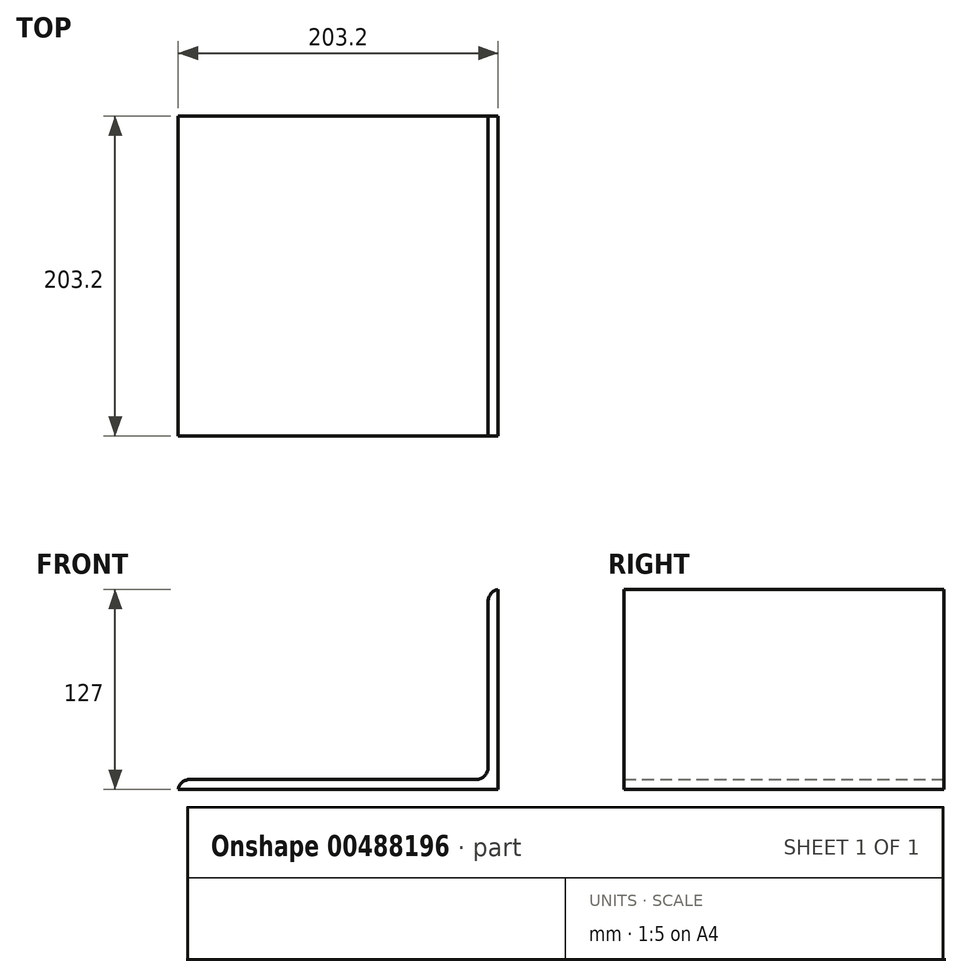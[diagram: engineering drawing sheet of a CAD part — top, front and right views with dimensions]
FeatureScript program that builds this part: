
annotation { "Feature Type Name" : "Feature", "Feature Type Description" : "" }
export const myFeature = defineFeature(function(context is Context, id is Id, definition is map)
    precondition{}
    {
        {
            var Q0;
            Q0=qCreatedBy(makeId("Front.planeOp"),FACE);
            var sketch = newSketch(context, id + "F0", { "sketchPlane" : qUnion([Q0])});
            skLineSegment(sketch, "E0", {"start": v(0, 0) * mm, "end": v(0, 127) * mm});
            skLineSegment(sketch, "E1", {"start": v(0, 127) * mm, "end": v(-6.35, 127) * mm});
            skLineSegment(sketch, "E2", {"start": v(-6.35, 127) * mm, "end": v(-6.35, 6.35) * mm});
            skLineSegment(sketch, "E3", {"start": v(-6.35, 6.35) * mm, "end": v(-203.2, 6.35) * mm});
            skLineSegment(sketch, "E4", {"start": v(-203.2, 6.35) * mm, "end": v(-203.2, 0) * mm});
            skLineSegment(sketch, "E5", {"start": v(-203.2, 0) * mm, "end": v(0, 0) * mm});
            skSolve(sketch);
        }
        {
            var Q0;
            Q0=makeQuery(id+"F0.imprint","IMPRINT",FACE,{"disambiguationData":[TD([[makeQuery(id+"F0.imprint","IMPRINT",EDGE,{"derivedFrom":sQuery(id+"F0.wireOp",EDGE,"E0")}),1.0]])]});
            extrude(context, id + "F1", {"entities" : qUnion([Q0]), "depth" : 203.2 * mm});
        }
        {
            var Q0;
            Q0=makeQuery(id+"F1.opExtrude","SWEPT_EDGE",EDGE,{"disambiguationData":[OSD([sQuery(id+"F0.wireOp",EDGE,"E1"),sQuery(id+"F0.wireOp",EDGE,"E2")])]});
            var Q1;
            Q1=makeQuery(id+"F1.opExtrude","SWEPT_EDGE",EDGE,{"disambiguationData":[OSD([sQuery(id+"F0.wireOp",EDGE,"E3"),sQuery(id+"F0.wireOp",EDGE,"E4")])]});
            var Q2;
            Q2=makeQuery(id+"F1.opExtrude","SWEPT_EDGE",EDGE,{"disambiguationData":[OSD([sQuery(id+"F0.wireOp",EDGE,"E2"),sQuery(id+"F0.wireOp",EDGE,"E3")])]});
            fillet(context, id + "F2", {"entities" : qUnion([Q0, Q1, Q2]), "radius" : 7.62 * mm, "tangentPropagation" : true, "allowEdgeOverflow" : false});
        }
    });
